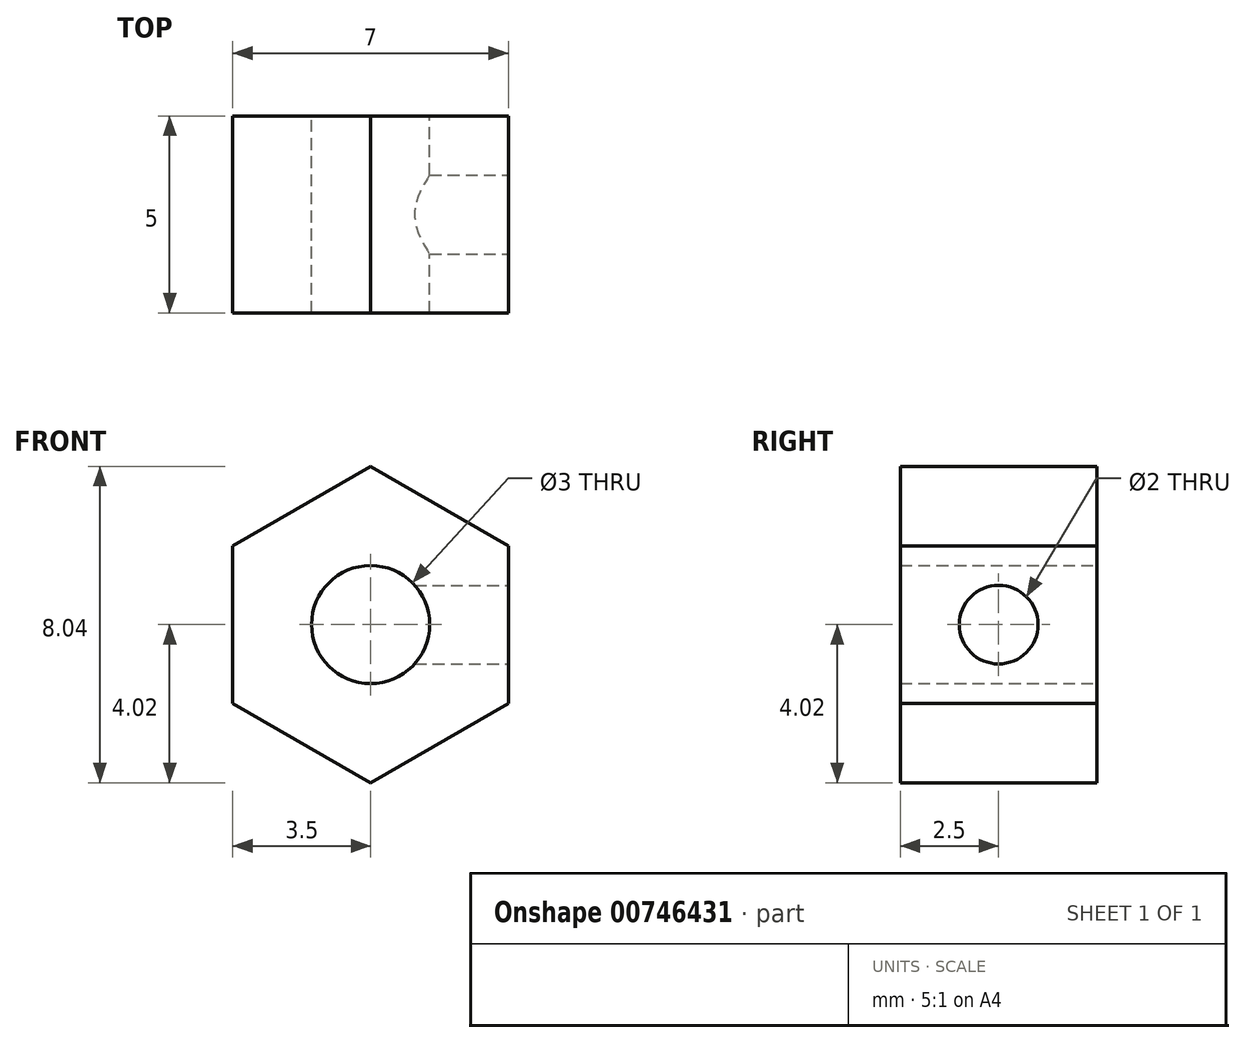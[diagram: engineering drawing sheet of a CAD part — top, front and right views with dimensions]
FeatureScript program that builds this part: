
annotation { "Feature Type Name" : "Feature", "Feature Type Description" : "" }
export const myFeature = defineFeature(function(context is Context, id is Id, definition is map)
    precondition{}
    {
        {
            var Q0;
            Q0=qCreatedBy(makeId("Top.planeOp"),FACE);
            var sketch = newSketch(context, id + "F0", { "sketchPlane" : qUnion([Q0])});
            skPoint(sketch, "E0.middle", {"position": v(0, 0) * mm});
            skLineSegment(sketch, "E1.bottom", {"start": v(-2, 3.5) * mm, "end": v(2, 3.5) * mm});
            skLineSegment(sketch, "E1.top", {"start": v(-2, -3.5) * mm, "end": v(2, -3.5) * mm});
            skPoint(sketch, "E2", {"position": v(0, 3.5) * mm});
            skLineSegment(sketch, "E3", {"start": v(-2, 3.5) * mm, "end": v(-4.02, 0) * mm});
            skLineSegment(sketch, "E4", {"start": v(-4.02, 0) * mm, "end": v(-2, -3.5) * mm});
            skLineSegment(sketch, "E5", {"start": v(2, -3.5) * mm, "end": v(4.02, 0) * mm});
            skLineSegment(sketch, "E6", {"start": v(4.02, 0) * mm, "end": v(2, 3.5) * mm});
            skCircle(sketch, "E7", {"center": v(0, 0) * mm, "radius": 1.5 * mm});
            skSolve(sketch);
        }
        {
            var Q0;
            Q0 = qSketchRegion(id + "F0", true);
            extrude(context, id + "F1", {"entities" : qUnion([Q0]), "depth" : 5 * mm, "offsetDistance" : 25.4 * mm});
        }
        {
            var Q0;
            Q0=makeQuery(id+"F1.opExtrude","SWEPT_FACE",FACE,{"disambiguationData":[OSD([sQuery(id+"F0.wireOp",EDGE,"E1.top")])]});
            var sketch = newSketch(context, id + "F2", { "sketchPlane" : qUnion([Q0])});
            skPoint(sketch, "E8", {"position": v(0, 2.5) * mm});
            skCircle(sketch, "E9", {"center": v(0, 2.5) * mm, "radius": 1 * mm});
            skSolve(sketch);
        }
        {
            var Q0;
            Q0 = qSketchRegion(id + "F2", true);
            extrude(context, id + "F3", {"entities" : qUnion([Q0]), "operationType" : NewBodyOperationType.REMOVE, "oppositeDirection" : true, "depth" : 3 * mm, "offsetDistance" : 25.4 * mm});
        }
        {
            var Q0;
            Q0=qCreatedBy(makeId("Top.planeOp"),FACE);
            var sketch = newSketch(context, id + "F4", { "sketchPlane" : qUnion([Q0])});
            skLineSegment(sketch, "E10", {"start": v(-17.32, 0) * mm, "end": v(21.39, 0) * mm});
            skSolve(sketch);
        }
        {
            var Q0;
            Q0=makeQuery(id+"F1.opExtrude","SWEPT_BODY",BODY,{"disambiguationData":[OSD([sQuery(id+"F0.wireOp",EDGE,"E1.bottom"),sQuery(id+"F0.wireOp",EDGE,"E1.top"),sQuery(id+"F0.wireOp",EDGE,"E3"),sQuery(id+"F0.wireOp",EDGE,"E4"),sQuery(id+"F0.wireOp",EDGE,"E5"),sQuery(id+"F0.wireOp",EDGE,"E6"),sQuery(id+"F0.wireOp",EDGE,"E7")])]});
            var Q1;
            Q1=sQuery(id+"F4.wireOp",EDGE,"E10");
            transform(context, id + "F5", {"entities" : qUnion([Q0]), "transformType" : TransformType.ROTATION, "transformAxis" : qUnion([Q1]), "angle" : 90 * degree, "makeCopy" : false});
        }
        {
            var Q0;
            Q0=qCreatedBy(makeId("Top.planeOp"),FACE);
            var sketch = newSketch(context, id + "F6", { "sketchPlane" : qUnion([Q0])});
            skLineSegment(sketch, "E11", {"start": v(0, 28.13) * mm, "end": v(0, -26.99) * mm});
            skSolve(sketch);
        }
        {
            var Q0;
            Q0=makeQuery(id+"F1.opExtrude","SWEPT_BODY",BODY,{"disambiguationData":[OSD([sQuery(id+"F0.wireOp",EDGE,"E1.bottom"),sQuery(id+"F0.wireOp",EDGE,"E1.top"),sQuery(id+"F0.wireOp",EDGE,"E3"),sQuery(id+"F0.wireOp",EDGE,"E4"),sQuery(id+"F0.wireOp",EDGE,"E5"),sQuery(id+"F0.wireOp",EDGE,"E6"),sQuery(id+"F0.wireOp",EDGE,"E7")])]});
            var Q1;
            Q1=sQuery(id+"F6.wireOp",EDGE,"E11");
            transform(context, id + "F7", {"entities" : qUnion([Q0]), "transformType" : TransformType.ROTATION, "transformAxis" : qUnion([Q1]), "angle" : 90 * degree, "makeCopy" : false});
        }
    });
